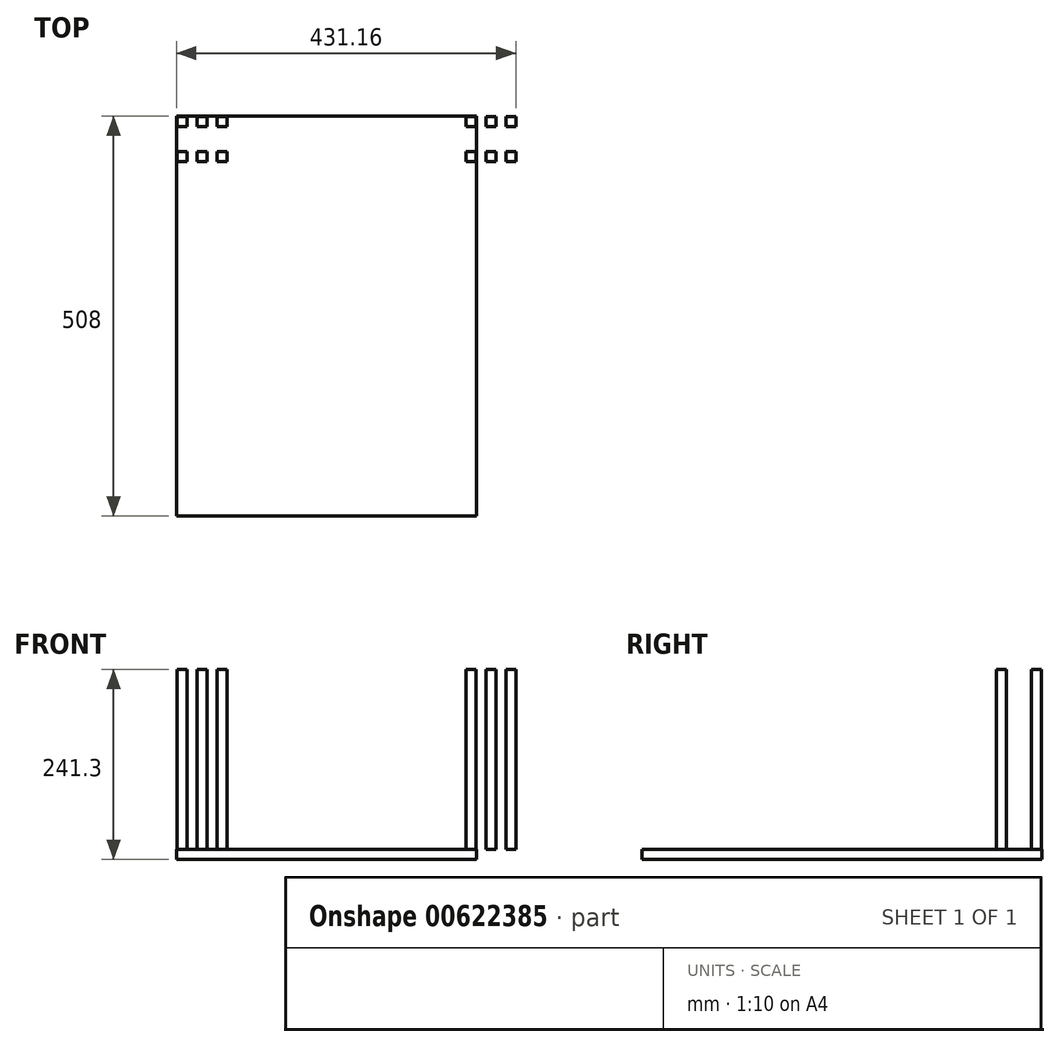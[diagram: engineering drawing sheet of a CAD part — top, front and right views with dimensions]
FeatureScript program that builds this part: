
annotation { "Feature Type Name" : "Feature", "Feature Type Description" : "" }
export const myFeature = defineFeature(function(context is Context, id is Id, definition is map)
    precondition{}
    {
        {
            var Q0;
            Q0=qCreatedBy(makeId("Top.planeOp"),FACE);
            var sketch = newSketch(context, id + "F0", { "sketchPlane" : qUnion([Q0])});
            skLineSegment(sketch, "E0.bottom", {"start": v(190.5, 254) * mm, "end": v(-190.5, 254) * mm});
            skLineSegment(sketch, "E0.top", {"start": v(190.5, -254) * mm, "end": v(-190.5, -254) * mm});
            skLineSegment(sketch, "E0.left", {"start": v(190.5, 254) * mm, "end": v(190.5, -254) * mm});
            skLineSegment(sketch, "E0.right", {"start": v(-190.5, 254) * mm, "end": v(-190.5, -254) * mm});
            skPoint(sketch, "E0.middle", {"position": v(0, 0) * mm});
            skSolve(sketch);
        }
        {
            var Q0;
            Q0 = qSketchRegion(id + "F0", true);
            extrude(context, id + "F1", {"entities" : qUnion([Q0]), "depth" : 12.7 * mm, "offsetDistance" : 25.4 * mm});
        }
        {
            var Q0;
            Q0=makeQuery(id+"F1.opExtrude","CAP_FACE",FACE,{"disambiguationData":[OSD([sQuery(id+"F0.wireOp",EDGE,"E0.bottom"),sQuery(id+"F0.wireOp",EDGE,"E0.top"),sQuery(id+"F0.wireOp",EDGE,"E0.left"),sQuery(id+"F0.wireOp",EDGE,"E0.right")])],"isStart":false});
            var sketch = newSketch(context, id + "F2", { "sketchPlane" : qUnion([Q0])});
            skLineSegment(sketch, "E1.bottom", {"start": v(-189.87, 253.37) * mm, "end": v(-177.17, 253.37) * mm});
            skLineSegment(sketch, "E1.top", {"start": v(-189.87, 240.67) * mm, "end": v(-177.17, 240.67) * mm});
            skLineSegment(sketch, "E1.left", {"start": v(-189.87, 253.37) * mm, "end": v(-189.87, 240.67) * mm});
            skLineSegment(sketch, "E1.right", {"start": v(-177.17, 253.37) * mm, "end": v(-177.17, 240.67) * mm});
            skLineSegment(sketch, "E2.bottom", {"start": v(189.87, 253.37) * mm, "end": v(177.17, 253.37) * mm});
            skLineSegment(sketch, "E2.top", {"start": v(189.87, 240.67) * mm, "end": v(177.17, 240.67) * mm});
            skLineSegment(sketch, "E2.left", {"start": v(189.87, 253.37) * mm, "end": v(189.87, 240.67) * mm});
            skLineSegment(sketch, "E2.right", {"start": v(177.17, 253.37) * mm, "end": v(177.17, 240.67) * mm});
            skLineSegment(sketch, "E3.0.1.0", {"start": v(-177.17, 209.17) * mm, "end": v(-177.17, 196.47) * mm});
            skLineSegment(sketch, "E3.0.1.1", {"start": v(-189.87, 196.47) * mm, "end": v(-177.17, 196.47) * mm});
            skLineSegment(sketch, "E3.0.1.2", {"start": v(-189.87, 209.17) * mm, "end": v(-189.87, 196.47) * mm});
            skLineSegment(sketch, "E3.0.1.3", {"start": v(-189.87, 209.17) * mm, "end": v(-177.17, 209.17) * mm});
            skLineSegment(sketch, "E3.0.1.4", {"start": v(189.87, 209.17) * mm, "end": v(189.87, 196.47) * mm});
            skLineSegment(sketch, "E3.0.1.5", {"start": v(189.87, 196.47) * mm, "end": v(177.17, 196.47) * mm});
            skLineSegment(sketch, "E3.0.1.6", {"start": v(189.87, 209.17) * mm, "end": v(177.17, 209.17) * mm});
            skLineSegment(sketch, "E3.0.1.7", {"start": v(177.17, 209.17) * mm, "end": v(177.17, 196.47) * mm});
            skLineSegment(sketch, "E3.1.0.0", {"start": v(-151.77, 253.37) * mm, "end": v(-151.77, 240.67) * mm});
            skLineSegment(sketch, "E3.1.0.1", {"start": v(-164.47, 240.67) * mm, "end": v(-151.77, 240.67) * mm});
            skLineSegment(sketch, "E3.1.0.2", {"start": v(-164.47, 253.37) * mm, "end": v(-164.47, 240.67) * mm});
            skLineSegment(sketch, "E3.1.0.3", {"start": v(-164.47, 253.37) * mm, "end": v(-151.77, 253.37) * mm});
            skLineSegment(sketch, "E3.1.0.4", {"start": v(215.27, 253.37) * mm, "end": v(215.27, 240.67) * mm});
            skLineSegment(sketch, "E3.1.0.5", {"start": v(215.27, 240.67) * mm, "end": v(202.57, 240.67) * mm});
            skLineSegment(sketch, "E3.1.0.6", {"start": v(215.27, 253.37) * mm, "end": v(202.57, 253.37) * mm});
            skLineSegment(sketch, "E3.1.0.7", {"start": v(202.57, 253.37) * mm, "end": v(202.57, 240.67) * mm});
            skLineSegment(sketch, "E3.1.1.0", {"start": v(-151.77, 209.17) * mm, "end": v(-151.77, 196.47) * mm});
            skLineSegment(sketch, "E3.1.1.1", {"start": v(-164.47, 196.47) * mm, "end": v(-151.77, 196.47) * mm});
            skLineSegment(sketch, "E3.1.1.2", {"start": v(-164.47, 209.17) * mm, "end": v(-164.47, 196.47) * mm});
            skLineSegment(sketch, "E3.1.1.3", {"start": v(-164.47, 209.17) * mm, "end": v(-151.77, 209.17) * mm});
            skLineSegment(sketch, "E3.1.1.4", {"start": v(215.27, 209.17) * mm, "end": v(215.27, 196.47) * mm});
            skLineSegment(sketch, "E3.1.1.5", {"start": v(215.27, 196.47) * mm, "end": v(202.57, 196.47) * mm});
            skLineSegment(sketch, "E3.1.1.6", {"start": v(215.27, 209.17) * mm, "end": v(202.57, 209.17) * mm});
            skLineSegment(sketch, "E3.1.1.7", {"start": v(202.57, 209.17) * mm, "end": v(202.57, 196.47) * mm});
            skLineSegment(sketch, "E3.2.0.0", {"start": v(-126.37, 253.37) * mm, "end": v(-126.37, 240.67) * mm});
            skLineSegment(sketch, "E3.2.0.1", {"start": v(-139.07, 240.67) * mm, "end": v(-126.37, 240.67) * mm});
            skLineSegment(sketch, "E3.2.0.2", {"start": v(-139.07, 253.37) * mm, "end": v(-139.07, 240.67) * mm});
            skLineSegment(sketch, "E3.2.0.3", {"start": v(-139.07, 253.37) * mm, "end": v(-126.37, 253.37) * mm});
            skLineSegment(sketch, "E3.2.0.4", {"start": v(240.67, 253.37) * mm, "end": v(240.67, 240.67) * mm});
            skLineSegment(sketch, "E3.2.0.5", {"start": v(240.67, 240.67) * mm, "end": v(227.97, 240.67) * mm});
            skLineSegment(sketch, "E3.2.0.6", {"start": v(240.67, 253.37) * mm, "end": v(227.97, 253.37) * mm});
            skLineSegment(sketch, "E3.2.0.7", {"start": v(227.97, 253.37) * mm, "end": v(227.97, 240.67) * mm});
            skLineSegment(sketch, "E3.2.1.0", {"start": v(-126.37, 209.17) * mm, "end": v(-126.37, 196.47) * mm});
            skLineSegment(sketch, "E3.2.1.1", {"start": v(-139.07, 196.47) * mm, "end": v(-126.37, 196.47) * mm});
            skLineSegment(sketch, "E3.2.1.2", {"start": v(-139.07, 209.17) * mm, "end": v(-139.07, 196.47) * mm});
            skLineSegment(sketch, "E3.2.1.3", {"start": v(-139.07, 209.17) * mm, "end": v(-126.37, 209.17) * mm});
            skLineSegment(sketch, "E3.2.1.4", {"start": v(240.67, 209.17) * mm, "end": v(240.67, 196.47) * mm});
            skLineSegment(sketch, "E3.2.1.5", {"start": v(240.67, 196.47) * mm, "end": v(227.97, 196.47) * mm});
            skLineSegment(sketch, "E3.2.1.6", {"start": v(240.67, 209.17) * mm, "end": v(227.97, 209.17) * mm});
            skLineSegment(sketch, "E3.2.1.7", {"start": v(227.97, 209.17) * mm, "end": v(227.97, 196.47) * mm});
            skLineSegment(sketch, "E3.direction1", {"start": v(-189.87, 240.67) * mm, "end": v(-164.47, 240.67) * mm, "construction": true});
            skLineSegment(sketch, "E3.direction2", {"start": v(-189.87, 240.67) * mm, "end": v(-189.87, 196.47) * mm, "construction": true});
            skSolve(sketch);
        }
        {
            var Q0;
            Q0 = qSketchRegion(id + "F2", true);
            extrude(context, id + "F3", {"entities" : qUnion([Q0]), "operationType" : NewBodyOperationType.ADD, "depth" : 228.6 * mm, "offsetDistance" : 25.4 * mm});
        }
    });
